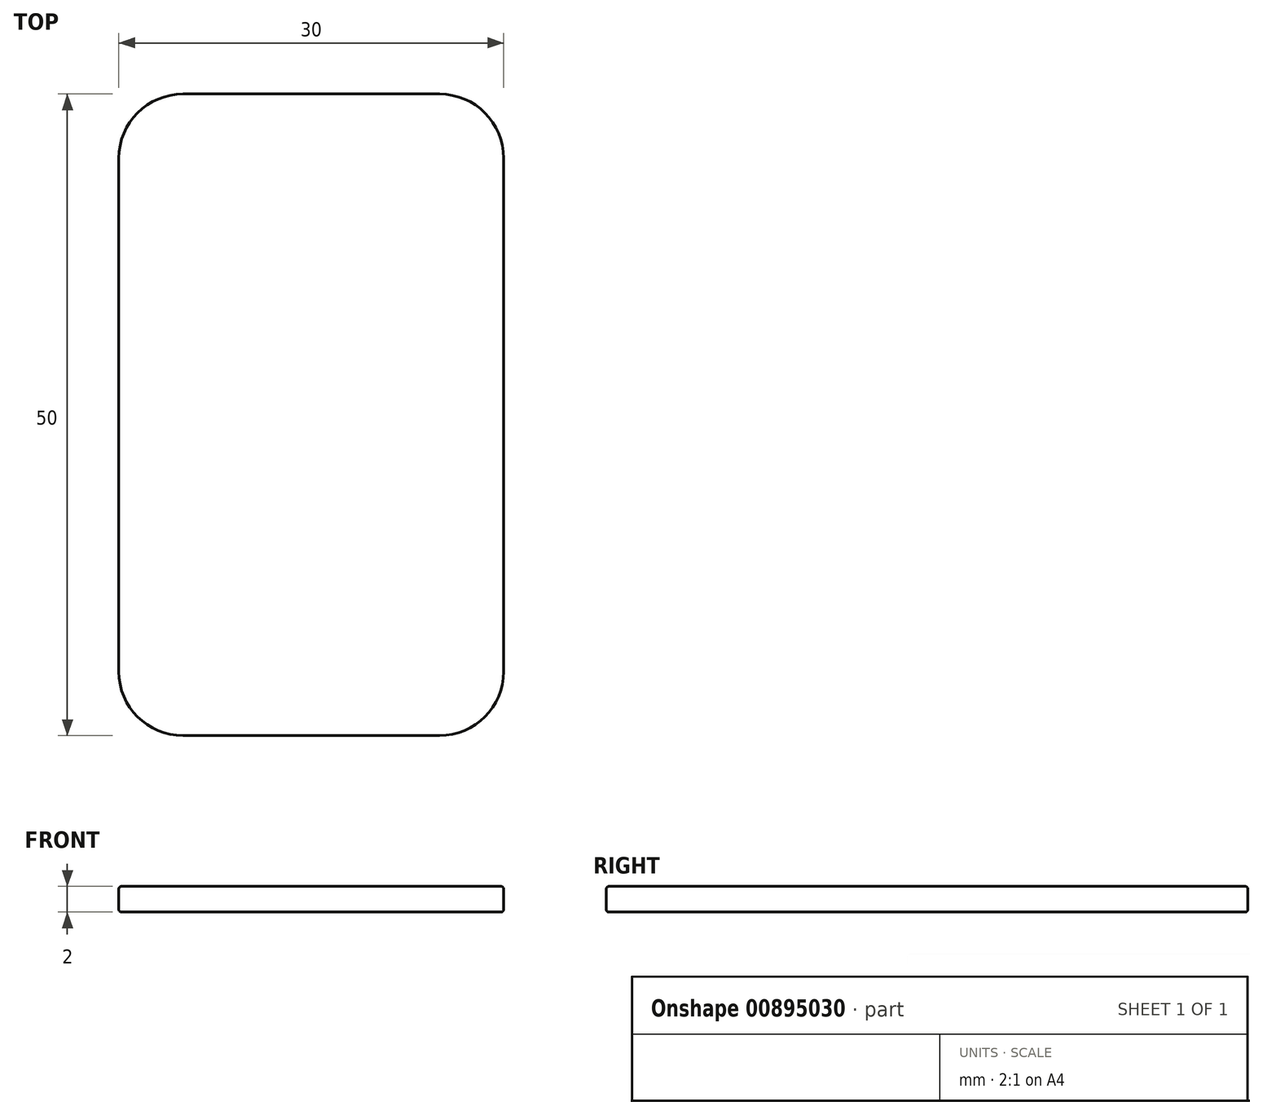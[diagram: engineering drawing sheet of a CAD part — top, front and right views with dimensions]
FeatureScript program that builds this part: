
annotation { "Feature Type Name" : "Feature", "Feature Type Description" : "" }
export const myFeature = defineFeature(function(context is Context, id is Id, definition is map)
    precondition{}
    {
        {
            var Q0;
            Q0=qCreatedBy(makeId("Top.planeOp"),FACE);
            var sketch = newSketch(context, id + "F0", { "sketchPlane" : qUnion([Q0])});
            skLineSegment(sketch, "E0.bottom", {"start": v(15, 25) * mm, "end": v(-15, 25) * mm});
            skLineSegment(sketch, "E0.top", {"start": v(15, -25) * mm, "end": v(-15, -25) * mm});
            skLineSegment(sketch, "E0.left", {"start": v(15, 25) * mm, "end": v(15, -25) * mm});
            skLineSegment(sketch, "E0.right", {"start": v(-15, 25) * mm, "end": v(-15, -25) * mm});
            skPoint(sketch, "E0.middle", {"position": v(0, 0) * mm});
            skSolve(sketch);
        }
        {
            var Q0;
            Q0=qSketchRegion(id+"F0",true);
            extrude(context, id + "F1", {"entities" : qUnion([Q0]), "depth" : 2 * mm, "offsetDistance" : 25 * mm});
        }
        {
            var Q0;
            Q0=makeQuery(id+"F1.opExtrude","SWEPT_EDGE",EDGE,{"disambiguationData":[OSD([sQuery(id+"F0.wireOp",EDGE,"E0.bottom"),sQuery(id+"F0.wireOp",EDGE,"E0.right")])]});
            var Q1;
            Q1=makeQuery(id+"F1.opExtrude","SWEPT_EDGE",EDGE,{"disambiguationData":[OSD([sQuery(id+"F0.wireOp",EDGE,"E0.bottom"),sQuery(id+"F0.wireOp",EDGE,"E0.left")])]});
            var Q2;
            Q2=makeQuery(id+"F1.opExtrude","SWEPT_EDGE",EDGE,{"disambiguationData":[OSD([sQuery(id+"F0.wireOp",EDGE,"E0.top"),sQuery(id+"F0.wireOp",EDGE,"E0.right")])]});
            var Q3;
            Q3=makeQuery(id+"F1.opExtrude","SWEPT_EDGE",EDGE,{"disambiguationData":[OSD([sQuery(id+"F0.wireOp",EDGE,"E0.top"),sQuery(id+"F0.wireOp",EDGE,"E0.left")])]});
            fillet(context, id + "F2", {"entities" : qUnion([Q0, Q1, Q2, Q3]), "radius" : 5 * mm, "tangentPropagation" : true, "allowEdgeOverflow" : false});
        }
        {
            var Q0;
            Q0=makeQuery(id+"F1.opExtrude","CAP_FACE",FACE,{"disambiguationData":[OSD([sQuery(id+"F0.wireOp",EDGE,"E0.bottom"),sQuery(id+"F0.wireOp",EDGE,"E0.top"),sQuery(id+"F0.wireOp",EDGE,"E0.left"),sQuery(id+"F0.wireOp",EDGE,"E0.right")])],"isStart":false});
            var Q1;
            Q1=makeQuery(id+"F1.opExtrude","CAP_FACE",FACE,{"disambiguationData":[OSD([sQuery(id+"F0.wireOp",EDGE,"E0.bottom"),sQuery(id+"F0.wireOp",EDGE,"E0.top"),sQuery(id+"F0.wireOp",EDGE,"E0.left"),sQuery(id+"F0.wireOp",EDGE,"E0.right")])],"isStart":true});
            fillet(context, id + "F3", {"entities" : qUnion([Q0, Q1]), "radius" : 0.2 * mm, "tangentPropagation" : true, "allowEdgeOverflow" : false});
        }
    });
